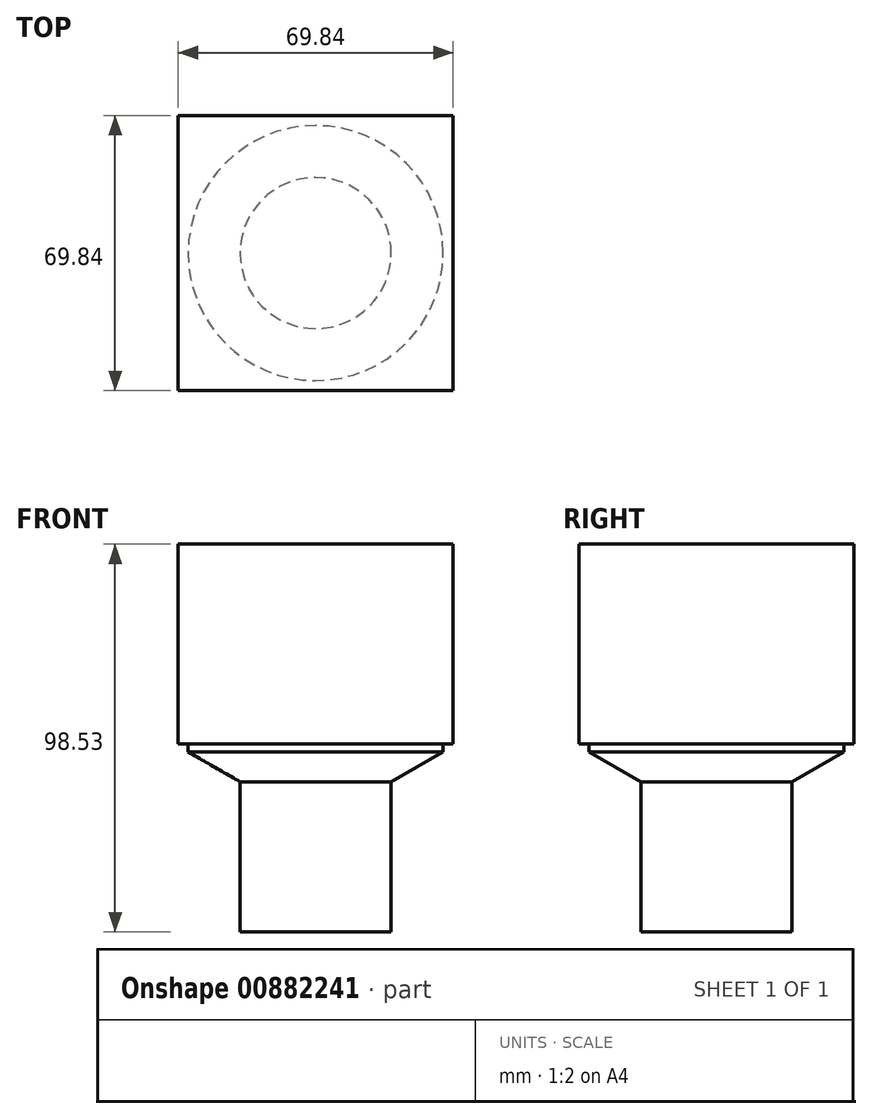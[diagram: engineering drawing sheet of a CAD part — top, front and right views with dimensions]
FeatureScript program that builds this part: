
annotation { "Feature Type Name" : "Feature", "Feature Type Description" : "" }
export const myFeature = defineFeature(function(context is Context, id is Id, definition is map)
    precondition{}
    {
        {
            var Q0;
            Q0=qCreatedBy(makeId("Front.planeOp"),FACE);
            var sketch = newSketch(context, id + "F0", { "sketchPlane" : qUnion([Q0])});
            skLineSegment(sketch, "E0", {"start": v(-34.93, 40.16) * mm, "end": v(32.4, 40.16) * mm});
            skLineSegment(sketch, "E1", {"start": v(32.4, 40.16) * mm, "end": v(32.4, 38.16) * mm});
            skLineSegment(sketch, "E2", {"start": v(32.4, 38.16) * mm, "end": v(19.2, 30.54) * mm});
            skLineSegment(sketch, "E3", {"start": v(19.2, 30.54) * mm, "end": v(19.2, -7.57) * mm});
            skLineSegment(sketch, "E4", {"start": v(19.2, -7.57) * mm, "end": v(0, -7.57) * mm});
            skLineSegment(sketch, "E5", {"start": v(0, -7.57) * mm, "end": v(0, 40.16) * mm});
            skLineSegment(sketch, "E6.bottom", {"start": v(-34.93, 40.16) * mm, "end": v(34.93, 40.16) * mm});
            skLineSegment(sketch, "E6.top", {"start": v(-34.93, 90.96) * mm, "end": v(34.93, 90.96) * mm});
            skLineSegment(sketch, "E6.left", {"start": v(-34.93, 40.16) * mm, "end": v(-34.93, 90.96) * mm});
            skLineSegment(sketch, "E6.right", {"start": v(34.92, 40.16) * mm, "end": v(34.92, 90.96) * mm});
            skSolve(sketch);
        }
        {
            var Q0;
            Q0=makeQuery(id+"F0.imprint","IMPRINT",FACE,{"disambiguationData":[TD([[makeQuery(id+"F0.imprint","IMPRINT",EDGE,{"derivedFrom":sQuery(id+"F0.wireOp",EDGE,"E1")}),-1.0]])]});
            var Q1;
            Q1=sQuery(id+"F0.wireOp",EDGE,"E5");
            revolve(context, id + "F1", {"surfaceOperationType" : NewSurfaceOperationType.NEW, "entities" : qUnion([Q0]), "axis" : qUnion([Q1]), "revolveType" : RevolveType.FULL});
        }
        {
            var Q0;
            Q0=makeQuery(id+"F0.imprint","IMPRINT",FACE,{"disambiguationData":[TD([[makeQuery(id+"F0.imprint","IMPRINT",EDGE,{"derivedFrom":sQuery(id+"F0.wireOp",EDGE,"E6.top")}),-1.0]])]});
            extrude(context, id + "F2", {"entities" : qUnion([Q0]), "operationType" : NewBodyOperationType.ADD, "depth" : 69.85 * mm, "offsetDistance" : 25.4 * mm, "symmetric" : true});
        }
    });
